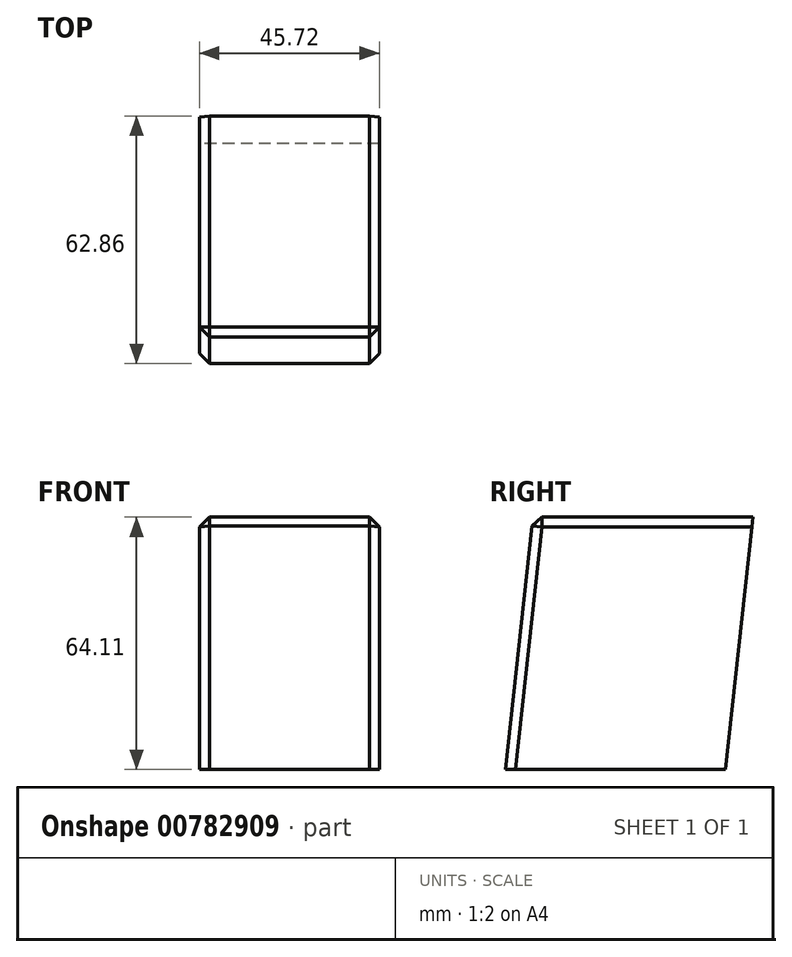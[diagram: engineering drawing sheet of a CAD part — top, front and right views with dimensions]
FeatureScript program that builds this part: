
annotation { "Feature Type Name" : "Feature", "Feature Type Description" : "" }
export const myFeature = defineFeature(function(context is Context, id is Id, definition is map)
    precondition{}
    {
        {
            var Q0;
            Q0=qCreatedBy(makeId("Right.planeOp"),FACE);
            var sketch = newSketch(context, id + "F0", { "sketchPlane" : qUnion([Q0])});
            skLineSegment(sketch, "E0", {"start": v(-41.28, -29.32) * mm, "end": v(-34.3, 34.8) * mm});
            skLineSegment(sketch, "E1", {"start": v(-34.3, 34.8) * mm, "end": v(21.58, 34.8) * mm});
            skLineSegment(sketch, "E2", {"start": v(21.58, 34.8) * mm, "end": v(14.6, -29.32) * mm});
            skLineSegment(sketch, "E3", {"start": v(14.6, -29.32) * mm, "end": v(-41.28, -29.32) * mm});
            skSolve(sketch);
        }
        {
            var Q0;
            Q0=makeQuery(id+"F0.imprint","IMPRINT",FACE,{"disambiguationData":[TD([[makeQuery(id+"F0.imprint","IMPRINT",EDGE,{"derivedFrom":sQuery(id+"F0.wireOp",EDGE,"E0")}),-1.0]])]});
            extrude(context, id + "F1", {"entities" : qUnion([Q0]), "depth" : 45.72 * mm, "offsetDistance" : 25.4 * mm});
        }
        {
            var Q0;
            Q0=makeQuery(id+"F1.opExtrude","SWEPT_EDGE",EDGE,{"disambiguationData":[OSD([sQuery(id+"F0.wireOp",EDGE,"E0"),sQuery(id+"F0.wireOp",EDGE,"E1")])]});
            var Q1;
            Q1=makeQuery(id+"F1.opExtrude","CAP_EDGE",EDGE,{"disambiguationData":[OSD([sQuery(id+"F0.wireOp",EDGE,"E1")])],"isStart":false});
            var Q2;
            Q2=makeQuery(id+"F1.opExtrude","CAP_EDGE",EDGE,{"disambiguationData":[OSD([sQuery(id+"F0.wireOp",EDGE,"E0")])],"isStart":false});
            var Q3;
            Q3=makeQuery(id+"F1.opExtrude","CAP_EDGE",EDGE,{"disambiguationData":[OSD([sQuery(id+"F0.wireOp",EDGE,"E0")])],"isStart":true});
            var Q4;
            Q4=makeQuery(id+"F1.opExtrude","CAP_EDGE",EDGE,{"disambiguationData":[OSD([sQuery(id+"F0.wireOp",EDGE,"E1")])],"isStart":true});
            chamfer(context, id + "F2", {"entities" : qUnion([Q0, Q1, Q2, Q3, Q4]), "width" : 2.54 * mm, "tangentPropagation" : true});
        }
    });
